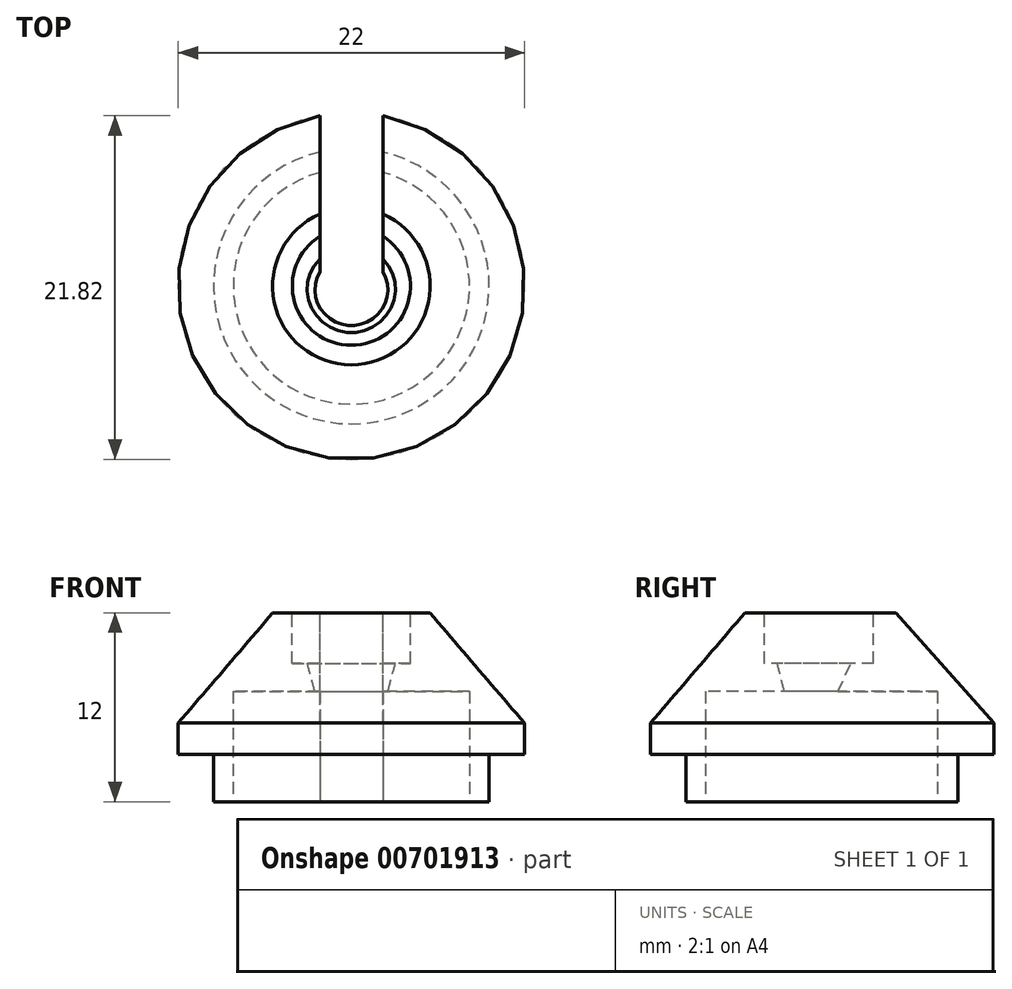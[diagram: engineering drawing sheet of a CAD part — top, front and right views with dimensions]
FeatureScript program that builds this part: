
annotation { "Feature Type Name" : "Feature", "Feature Type Description" : "" }
export const myFeature = defineFeature(function(context is Context, id is Id, definition is map)
    precondition{}
    {
        {
            var Q0;
            Q0=qCreatedBy(makeId("Top.planeOp"),FACE);
            var sketch = newSketch(context, id + "F0", { "sketchPlane" : qUnion([Q0])});
            skArc(sketch, "E0", {"start": v(-2, 10.82) * mm, "mid": v(0, -11) * mm, "end": v(2, 10.82) * mm});
            skArc(sketch, "E1", {"start": v(-2, 8.52) * mm, "mid": v(0, -8.75) * mm, "end": v(2, 8.52) * mm});
            skArc(sketch, "E2", {"start": v(-2, 0) * mm, "mid": v(0, -2) * mm, "end": v(2, 0) * mm});
            skLineSegment(sketch, "E3", {"start": v(-2, 0) * mm, "end": v(-2, 10.82) * mm});
            skLineSegment(sketch, "E4", {"start": v(2, 0) * mm, "end": v(2, 10.82) * mm});
            skCircle(sketch, "E5", {"center": v(0, 0) * mm, "radius": 7.5 * mm});
            skSolve(sketch);
        }
        {
            var Q0;
            {var subQ0=sQuery(id+"F0.wireOp",EDGE,"E1");Q0=makeQuery(id+"F0.imprint","IMPRINT",FACE,{"disambiguationData":[TD([[makeQuery(id+"F0.imprint","IMPRINT",EDGE,{"derivedFrom":subQ0}),1.0]])]});}
            var Q1;
            {var subQ0=sQuery(id+"F0.wireOp",EDGE,"E0");Q1=makeQuery(id+"F0.imprint","IMPRINT",FACE,{"disambiguationData":[TD([[makeQuery(id+"F0.imprint","IMPRINT",EDGE,{"derivedFrom":subQ0}),1.0]])]});}
            var Q2;
            {var subQ0=sQuery(id+"F0.wireOp",EDGE,"E2");Q2=makeQuery(id+"F0.imprint","IMPRINT",FACE,{"disambiguationData":[TD([[makeQuery(id+"F0.imprint","IMPRINT",EDGE,{"derivedFrom":subQ0}),-1.0]])]});}
            extrude(context, id + "F1", {"entities" : qUnion([Q0, Q1, Q2]), "depth" : 5 * mm, "offsetDistance" : 25 * mm});
        }
        {
            var Q0;
            Q0=qCreatedBy(makeId("Top.planeOp"),FACE);
            cPlane(context, id + "F2", {"entities" : qUnion([Q0]), "cplaneType" : CPlaneType.OFFSET, "offset" : 12 * mm, "width" : 150 * mm, "height" : 150 * mm});
        }
        {
            var Q0;
            Q0=qCreatedBy(id+"F2.planeOp",FACE);
            var sketch = newSketch(context, id + "F3", { "sketchPlane" : qUnion([Q0])});
            skPoint(sketch, "E6.0", {"position": v(0, 0) * mm});
            skArc(sketch, "E7", {"start": v(-2, 0) * mm, "mid": v(0, -2) * mm, "end": v(2, 0) * mm});
            skLineSegment(sketch, "E8", {"start": v(-2, 4.58) * mm, "end": v(-2, 0) * mm});
            skLineSegment(sketch, "E9", {"start": v(2, 4.58) * mm, "end": v(2, 0) * mm});
            skArc(sketch, "E10", {"start": v(-2, 4.58) * mm, "mid": v(0, -5) * mm, "end": v(2, 4.58) * mm});
            skArc(sketch, "E11", {"start": v(-2, 3.17) * mm, "mid": v(0, -3.75) * mm, "end": v(2, 3.17) * mm});
            skSolve(sketch);
        }
        {
            var Q1;
            Q1=makeQuery(id+"F1.opExtrude","CAP_FACE",FACE,{"disambiguationData":[OSD([sQuery(id+"F0.wireOp",EDGE,"E0"),sQuery(id+"F0.wireOp",EDGE,"E2"),sQuery(id+"F0.wireOp",EDGE,"E3"),sQuery(id+"F0.wireOp",EDGE,"E4")])],"isStart":false});
            var Q2;
            {var subQ0=sQuery(id+"F3.wireOp",EDGE,"E10");Q2=makeQuery(id+"F3.imprint","IMPRINT",FACE,{"disambiguationData":[TD([[makeQuery(id+"F3.imprint","IMPRINT",EDGE,{"derivedFrom":subQ0}),1.0]])]});}
            loft(context, id + "F4", {"operationType" : NewBodyOperationType.ADD, "sheetProfilesArray" : [{ "sheetProfileEntities" : qUnion([Q1]) }, { "sheetProfileEntities" : qUnion([Q2]) }]});
        }
        {
            var Q0;
            {var subQ0=sQuery(id+"F0.wireOp",EDGE,"E0");Q0=makeQuery(id+"F0.imprint","IMPRINT",FACE,{"disambiguationData":[TD([[makeQuery(id+"F0.imprint","IMPRINT",EDGE,{"derivedFrom":subQ0}),1.0]])]});}
            extrude(context, id + "F5", {"entities" : qUnion([Q0]), "operationType" : NewBodyOperationType.REMOVE, "depth" : 3 * mm, "offsetDistance" : 25 * mm});
        }
        {
            var Q0;
            {var subQ0=sQuery(id+"F3.wireOp",EDGE,"E7");Q0=makeQuery(id+"F3.imprint","IMPRINT",FACE,{"disambiguationData":[TD([[makeQuery(id+"F3.imprint","IMPRINT",EDGE,{"derivedFrom":subQ0}),-1.0]])]});}
            extrude(context, id + "F6", {"entities" : qUnion([Q0]), "operationType" : NewBodyOperationType.REMOVE, "oppositeDirection" : true, "depth" : 3.2 * mm, "offsetDistance" : 25 * mm});
        }
        {
            var Q0;
            {var subQ0=sQuery(id+"F0.wireOp",EDGE,"E2");Q0=makeQuery(id+"F0.imprint","IMPRINT",FACE,{"disambiguationData":[TD([[makeQuery(id+"F0.imprint","IMPRINT",EDGE,{"derivedFrom":subQ0}),-1.0]])]});}
            extrude(context, id + "F7", {"entities" : qUnion([Q0]), "operationType" : NewBodyOperationType.REMOVE, "depth" : 7 * mm, "offsetDistance" : 25 * mm});
        }
    });
